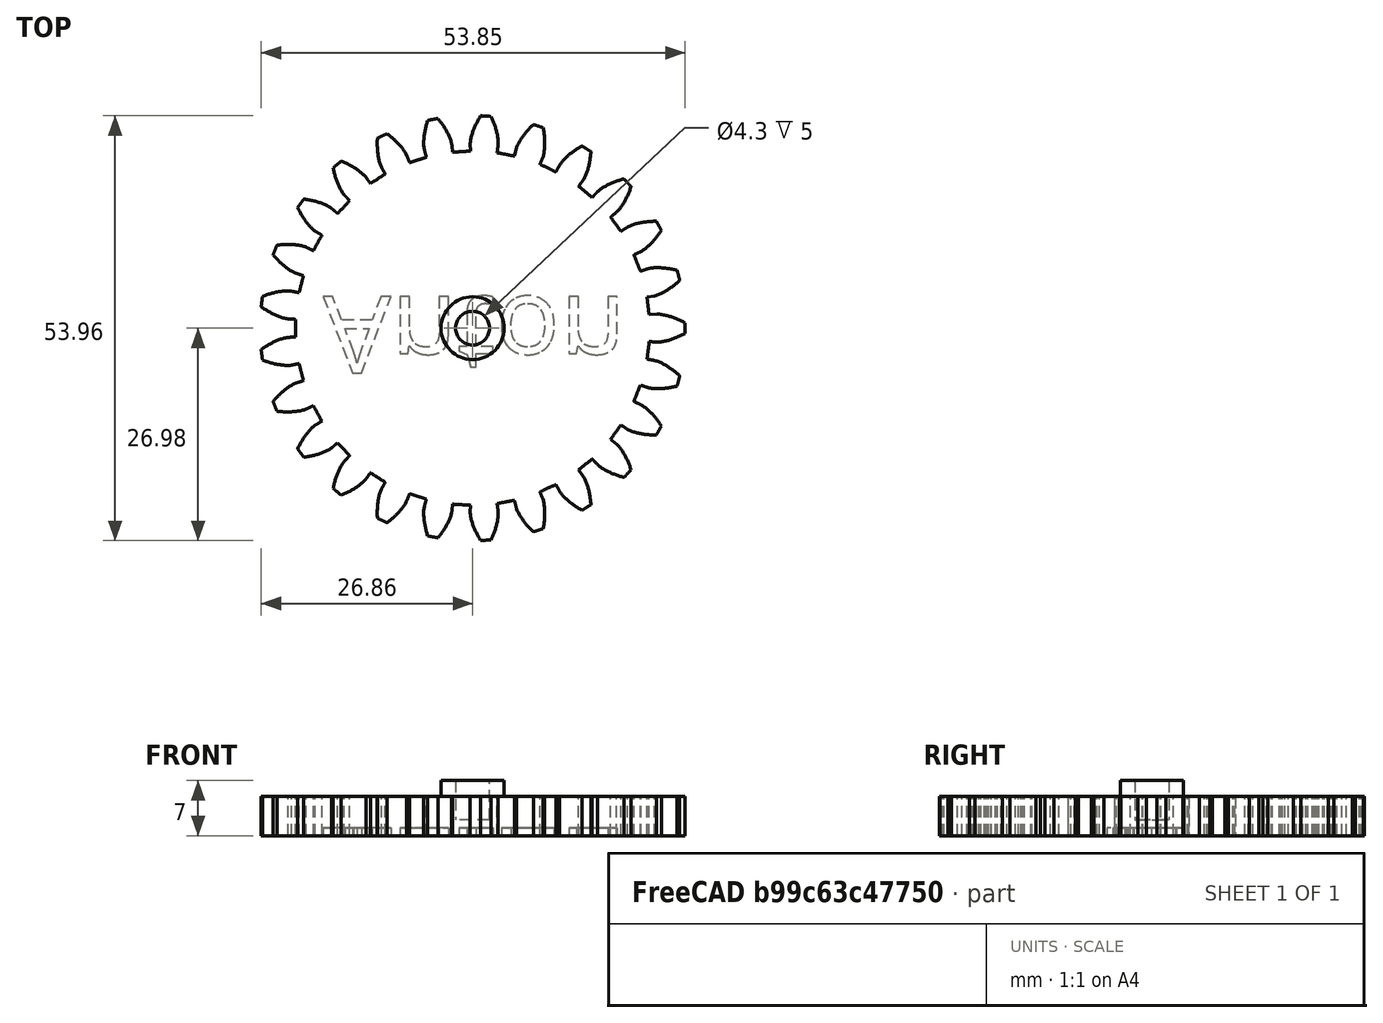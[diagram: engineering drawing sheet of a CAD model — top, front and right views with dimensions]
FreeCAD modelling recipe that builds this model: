
FCSTD DOCUMENT  (FreeCAD 0.21R33694 (Git))
Label: gear
License: All rights reserved
LicenseURL: http://en.wikipedia.org/wiki/All_rights_reserved
objects: Part::Cylinder×2, Part::Cut×2, Spreadsheet::Sheet×1, Part::FeaturePython×1, Part::Fuse×1, Part::Part2DObjectPython×1, Part::Extrusion×1
note: 8 computed .brp shape members not serialized (recipe doc carries the construction recipe); baked Part::Feature solids carry a one-line shape summary decoded from their .brp

FEATURE [Spreadsheet::Sheet] Spreadsheet  label="settings"
  cells = A1='Gear info; C1='Axle; E1='Hole; G1='Text; A2='Module size; B2(gear_module)=2; C2='Diameter; D2(axle_diameter)=8; E2='Diameter; F2(hole_dia)=4.3; G2='String; H2(text_string)='Test; A3='Teeth; B3(gear_teeth)=25; C3='Length; D3(axle_length)=2; E3='Depth; F3(hole_depth)=5; G3='Size; H3(text_size)=10; A4='height; B4(gear_height)=5; G4='Depth; H4(text_depth)=1; A8='Computed; A9='Circumference; A10='total axle length; B10(total_axle_length)==gear_height + axle_length
FEATURE [Part::FeaturePython] InvoluteGear  # WARN: FeaturePython — macro-defined, semantics opaque (R4)
  AttacherType = Attacher::AttachEngine3D
  angular_backlash = 0.229183
  backlash = 0.1
  beta = 0
  clearance = 0.25
  da = 54
  df = 45
  double_helix = false
  dw = 50
  head = 0
  head_fillet = 0
  height = 5
  module = 2
  numpoints = 6
  pressure_angle = 20
  properties_from_tool = false
  reversed_backlash = false
  root_fillet = 0
  shift = 0
  simple = false
  teeth = 25
  transverse_pitch = 6.28319
  traverse_module = 2
  undercut = false
  version = 0.0.4
  expr: angular_backlash = backlash / dw * 360 ° / pi
  expr: height = <<settings>>.gear_height
  expr: module = <<settings>>.gear_module
  expr: teeth = <<settings>>.gear_teeth
FEATURE [Part::Cylinder] Cylinder  label="axle_body"
  Angle = 360
  AttacherType = Attacher::AttachEngine3D
  FirstAngle = 0
  Height = 7
  Radius = 4
  SecondAngle = 0
  expr: Height = <<settings>>.total_axle_length
  expr: Radius = <<settings>>.axle_diameter / 2
FEATURE [Part::Cylinder] Cylinder001
  Angle = 360
  AttacherType = Attacher::AttachEngine3D
  FirstAngle = 0
  Height = 5
  Placement = pos=(0,0,2) rot=(0,0,1;0rad)
  Radius = 2.15
  SecondAngle = 0
  expr: .Placement.Base.x = 0
  expr: .Placement.Base.z = <<settings>>.total_axle_length - <<settings>>.hole_depth
  expr: Height = <<settings>>.hole_depth
  expr: Radius = <<settings>>.hole_dia / 2
FEATURE [Part::Fuse] Fusion
  Base = -> InvoluteGear
  Tool = -> Cylinder
FEATURE [Part::Cut] Cut
  Base = -> Fusion
  Tool = -> Cylinder001
FEATURE [Part::Part2DObjectPython] ShapeString  # Draft 2D object (typed FeaturePython)
  FontFile = <path>
  MakeFace = true
  Placement = pos=(-19,4,0) rot=(1,0,0;3.14159rad)
  Size = 6
  String = Anton
  Tracking = 0
FEATURE [Part::Extrusion] Extrude
  Base = -> ShapeString
  Dir = (0,0,-1)
  DirMode = 2
  FaceMakerClass = Part::FaceMakerBullseye
  LengthFwd = 0
  LengthRev = 1
  Solid = false
  Symmetric = false
FEATURE [Part::Cut] Cut001  label="named_gear"
  Base = -> Cut
  Tool = -> Extrude
note: 1 file-system path scrubbed to <path> (originals preserved in the JSON sidecar)
